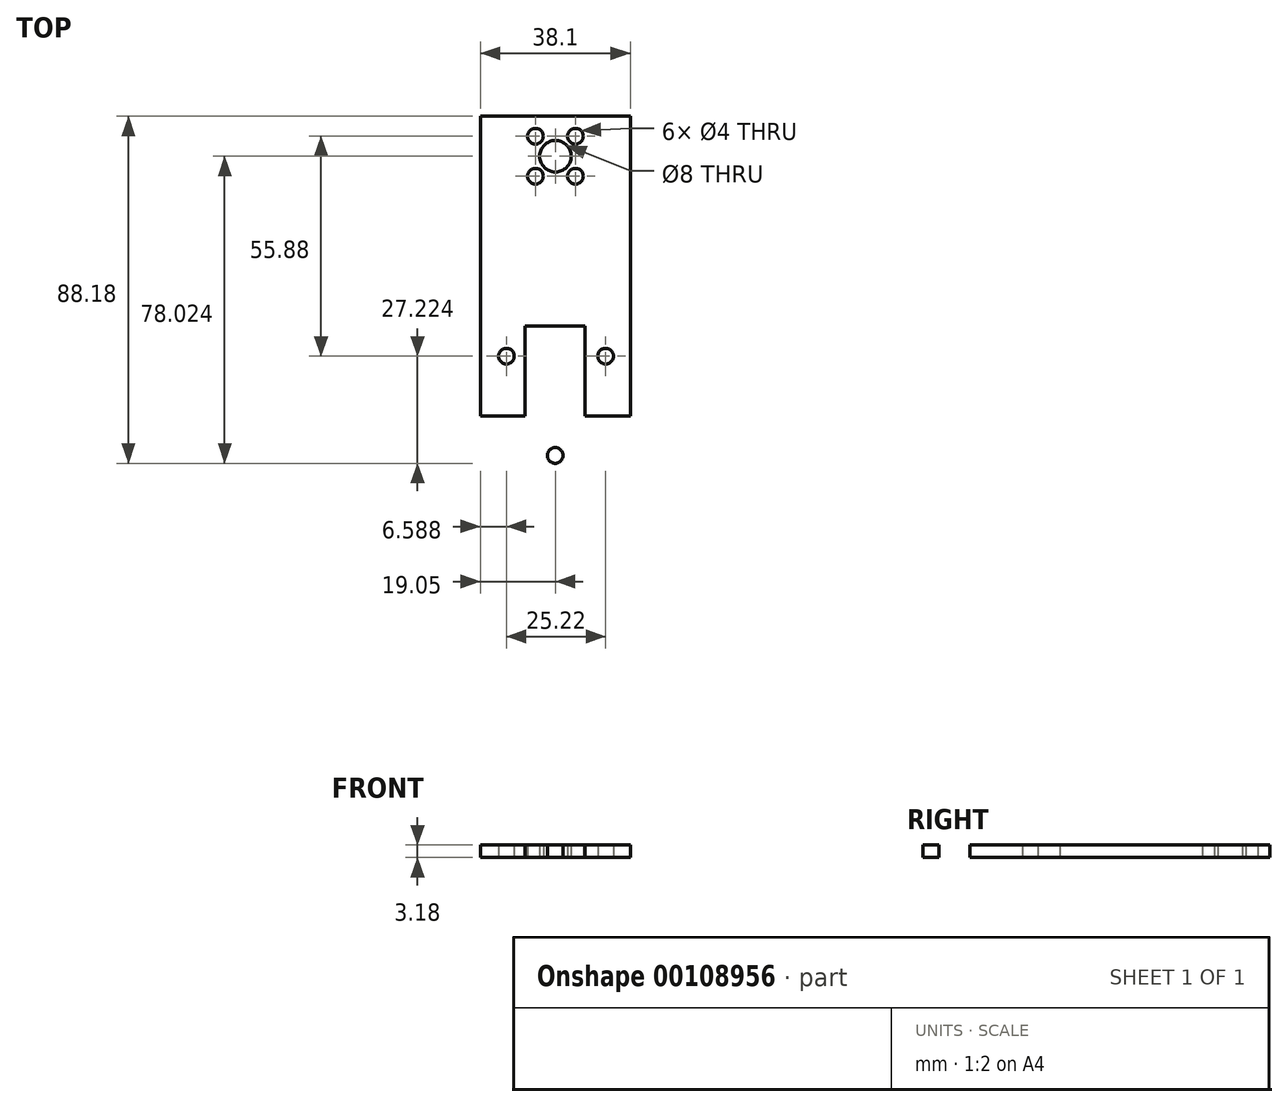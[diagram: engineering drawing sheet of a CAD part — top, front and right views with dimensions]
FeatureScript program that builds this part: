
annotation { "Feature Type Name" : "Feature", "Feature Type Description" : "" }
export const myFeature = defineFeature(function(context is Context, id is Id, definition is map)
    precondition{}
    {
        {
            var Q0;
            Q0=qCreatedBy(makeId("Top.planeOp"),FACE);
            var sketch = newSketch(context, id + "F0", { "sketchPlane" : qUnion([Q0])});
            skLineSegment(sketch, "E0.bottom", {"start": v(-19.05, 0.04) * mm, "end": v(19.05, 0.04) * mm});
            skLineSegment(sketch, "E0.top", {"start": v(-19.05, 76.24) * mm, "end": v(19.05, 76.24) * mm});
            skLineSegment(sketch, "E0.left", {"start": v(-19.05, 0.04) * mm, "end": v(-19.05, 76.24) * mm});
            skLineSegment(sketch, "E0.right", {"start": v(19.05, 0.04) * mm, "end": v(19.05, 76.24) * mm});
            skCircle(sketch, "E1", {"center": v(0, 66.08) * mm, "radius": 4 * mm});
            skCircle(sketch, "E2", {"center": v(-5.08, 71.16) * mm, "radius": 2 * mm});
            skCircle(sketch, "E3", {"center": v(-5.08, 61) * mm, "radius": 2 * mm});
            skCircle(sketch, "E4", {"center": v(5.08, 71.16) * mm, "radius": 2 * mm});
            skCircle(sketch, "E5", {"center": v(5.08, 61) * mm, "radius": 2 * mm});
            skLineSegment(sketch, "E6.bottom", {"start": v(-7.68, 22.9) * mm, "end": v(7.56, 22.9) * mm});
            skLineSegment(sketch, "E6.top", {"start": v(-7.68, 0.04) * mm, "end": v(7.56, 0.04) * mm});
            skLineSegment(sketch, "E6.left", {"start": v(-7.68, 22.9) * mm, "end": v(-7.68, 0.04) * mm});
            skLineSegment(sketch, "E6.right", {"start": v(7.56, 22.9) * mm, "end": v(7.56, 0.04) * mm});
            skCircle(sketch, "E7", {"center": v(12.76, 15.28) * mm, "radius": 2 * mm});
            skCircle(sketch, "E8", {"center": v(-12.46, 15.28) * mm, "radius": 2 * mm});
            skCircle(sketch, "E9", {"center": v(-0.06, -9.94) * mm, "radius": 2 * mm});
            skSolve(sketch);
        }
        {
            var Q0;
            Q0=qCreatedBy(makeId("Top.planeOp"),FACE);
            var sketch = newSketch(context, id + "F1", { "sketchPlane" : qUnion([Q0])});
            skLineSegment(sketch, "E10.bottom", {"start": v(-7.62, 22.9) * mm, "end": v(7.62, 22.9) * mm});
            skLineSegment(sketch, "E10.top", {"start": v(-7.62, 0.04) * mm, "end": v(7.62, 0.04) * mm});
            skLineSegment(sketch, "E10.left", {"start": v(-7.62, 22.9) * mm, "end": v(-7.62, 0.04) * mm});
            skLineSegment(sketch, "E10.right", {"start": v(7.62, 22.9) * mm, "end": v(7.62, 0.04) * mm});
            skCircle(sketch, "E11", {"center": v(12.82, 11.4) * mm, "radius": 2 * mm});
            skCircle(sketch, "E12", {"center": v(-12.4, 12.26) * mm, "radius": 2 * mm});
            skCircle(sketch, "E13", {"center": v(0, 0) * mm, "radius": 2 * mm});
            skSolve(sketch);
        }
        {
            var Q0;
            Q0=makeQuery(id+"F0.imprint","IMPRINT",FACE,{"disambiguationData":[TD([[makeQuery(id+"F0.imprint","IMPRINT",EDGE,{"derivedFrom":sQuery(id+"F0.wireOp",EDGE,"E9")}),1.0]])]});
            var Q1;
            Q1=makeQuery(id+"F0.imprint","IMPRINT",FACE,{"disambiguationData":[TD([[makeQuery(id+"F0.imprint","IMPRINT",EDGE,{"derivedFrom":sQuery(id+"F0.wireOp",EDGE,"E0.top")}),-1.0]])]});
            extrude(context, id + "F2", {"entities" : qUnion([Q0, Q1]), "depth" : 3.17 * mm});
        }
    });
